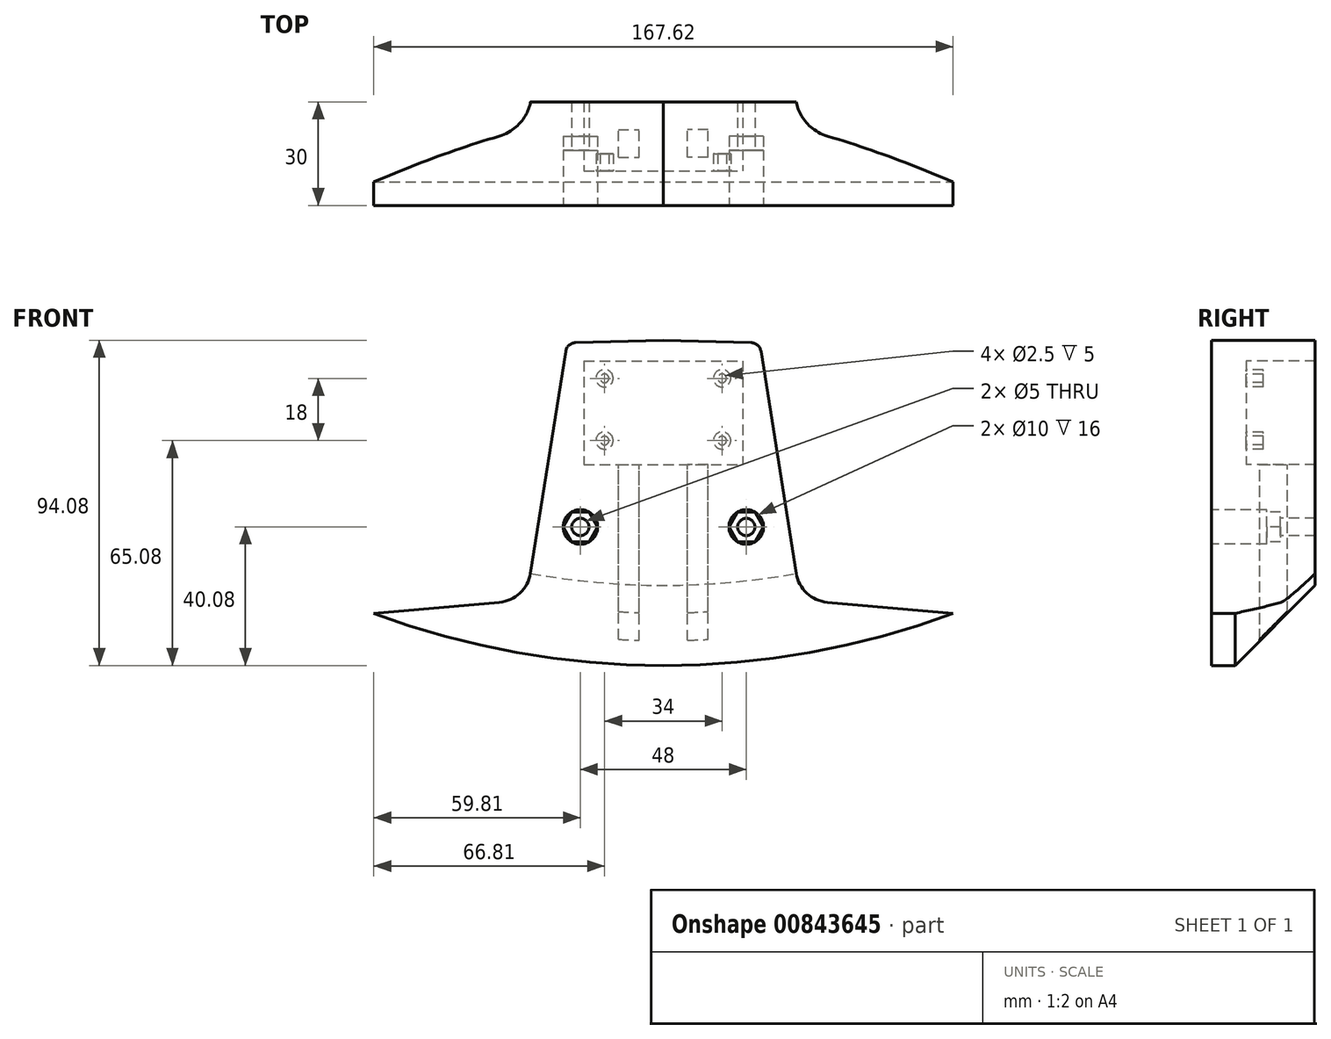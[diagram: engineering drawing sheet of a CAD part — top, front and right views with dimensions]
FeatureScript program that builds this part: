
annotation { "Feature Type Name" : "Feature", "Feature Type Description" : "" }
export const myFeature = defineFeature(function(context is Context, id is Id, definition is map)
    precondition{}
    {
        {
            var Q0;
            Q0=qCreatedBy(makeId("Front.planeOp"),FACE);
            var sketch = newSketch(context, id + "F0", { "sketchPlane" : qUnion([Q0])});
            skLineSegment(sketch, "E0.0", {"start": v(0, 104) * mm, "end": v(-25.36, 103.34) * mm});
            skLineSegment(sketch, "E1.0", {"start": v(-28.25, 100.8) * mm, "end": v(-38.45, 36.6) * mm});
            skArc(sketch, "E2.0", {"start": v(-38.45, 36.6) * mm, "mid": v(-41.51, 30.86) * mm, "end": v(-47.46, 28.21) * mm});
            skLineSegment(sketch, "E3.0", {"start": v(-47.46, 28.21) * mm, "end": v(-83.81, 25.03) * mm});
            skArc(sketch, "E4.0", {"start": v(-83.81, 25.03) * mm, "mid": v(-89.03, 27.33) * mm, "end": v(-89.9, 32.97) * mm});
            skLineSegment(sketch, "E5.0", {"start": v(-89.9, 32.97) * mm, "end": v(-64.25, 103.44) * mm});
            skArc(sketch, "E6", {"start": v(-105.92, 7.32) * mm, "mid": v(-53.83, -7.13) * mm, "end": v(0, -12) * mm});
            skArc(sketch, "E7", {"start": v(-25.36, 103.34) * mm, "mid": v(-27.26, 102.6) * mm, "end": v(-28.25, 100.8) * mm});
            skArc(sketch, "E8", {"start": v(-120, 37.98) * mm, "mid": v(-119.26, 19.76) * mm, "end": v(-105.92, 7.32) * mm});
            skLineSegment(sketch, "E9", {"start": v(-92.44, 113.7) * mm, "end": v(-64.25, 103.44) * mm});
            skArc(sketch, "E10.MirrorCS", {"start": v(25.36, 103.34) * mm, "mid": v(27.26, 102.6) * mm, "end": v(28.25, 100.8) * mm});
            skArc(sketch, "E11.MirrorCS", {"start": v(120, 37.98) * mm, "mid": v(119.26, 19.76) * mm, "end": v(105.92, 7.32) * mm});
            skLineSegment(sketch, "E12.MirrorCS", {"start": v(47.46, 28.21) * mm, "end": v(83.81, 25.03) * mm});
            skLineSegment(sketch, "E13.MirrorCS", {"start": v(0, 104) * mm, "end": v(25.36, 103.34) * mm});
            skLineSegment(sketch, "E14.MirrorCS", {"start": v(28.25, 100.8) * mm, "end": v(38.45, 36.6) * mm});
            skArc(sketch, "E15.MirrorCS", {"start": v(83.81, 25.03) * mm, "mid": v(89.03, 27.33) * mm, "end": v(89.9, 32.97) * mm});
            skArc(sketch, "E16.MirrorCS", {"start": v(38.45, 36.6) * mm, "mid": v(41.51, 30.86) * mm, "end": v(47.46, 28.21) * mm});
            skLineSegment(sketch, "E17.MirrorCS", {"start": v(89.9, 32.97) * mm, "end": v(64.25, 103.44) * mm});
            skArc(sketch, "E18.MirrorCS", {"start": v(105.92, 7.32) * mm, "mid": v(53.83, -7.13) * mm, "end": v(0, -12) * mm});
            skLineSegment(sketch, "E19.MirrorCS", {"start": v(92.44, 113.7) * mm, "end": v(64.25, 103.44) * mm});
            skLineSegment(sketch, "E20", {"start": v(-92.44, 113.7) * mm, "end": v(-120, 37.98) * mm});
            skLineSegment(sketch, "E21.MirrorCS", {"start": v(92.44, 113.7) * mm, "end": v(120, 37.98) * mm});
            skPoint(sketch, "E22", {"position": v(24, 50) * mm});
            skPoint(sketch, "E23", {"position": v(-24, 50) * mm});
            skLineSegment(sketch, "E24.bottom", {"start": v(-23, 98) * mm, "end": v(23, 98) * mm});
            skLineSegment(sketch, "E24.top", {"start": v(-23, 68) * mm, "end": v(23, 68) * mm});
            skLineSegment(sketch, "E24.left", {"start": v(-23, 98) * mm, "end": v(-23, 68) * mm});
            skLineSegment(sketch, "E24.right", {"start": v(23, 98) * mm, "end": v(23, 68) * mm});
            skCircle(sketch, "E25", {"center": v(17, 93) * mm, "radius": 2.5 * mm});
            skCircle(sketch, "E26", {"center": v(17, 75) * mm, "radius": 2.5 * mm});
            skCircle(sketch, "E27", {"center": v(-17, 93) * mm, "radius": 2.5 * mm});
            skCircle(sketch, "E28", {"center": v(-17, 75) * mm, "radius": 2.5 * mm});
            skCircle(sketch, "E29", {"center": v(17, 93) * mm, "radius": 1.25 * mm});
            skCircle(sketch, "E30", {"center": v(17, 75) * mm, "radius": 1.25 * mm});
            skCircle(sketch, "E31", {"center": v(-17, 75) * mm, "radius": 1.25 * mm});
            skCircle(sketch, "E32", {"center": v(-17, 93) * mm, "radius": 1.25 * mm});
            skPoint(sketch, "E33", {"position": v(0, 50) * mm});
            skArc(sketch, "E34", {"start": v(-83.81, 25.03) * mm, "mid": v(0, 9.92) * mm, "end": v(83.81, 25.03) * mm});
            skSolve(sketch);
        }
        {
            var Q0;
            Q0=makeQuery(id+"F0.imprint","IMPRINT",FACE,{"disambiguationData":[TD([[makeQuery(id+"F0.imprint","IMPRINT",EDGE,{"derivedFrom":sQuery(id+"F0.wireOp",EDGE,"E0.0")}),1.0]])]});
            var Q1;
            Q1=makeQuery(id+"F0.imprint","IMPRINT",FACE,{"disambiguationData":[TD([[makeQuery(id+"F0.imprint","IMPRINT",EDGE,{"derivedFrom":sQuery(id+"F0.wireOp",EDGE,"HJohPhqk-gpzc-Xpna-ZfSw-4RcINLic6Jsf")}),1.0]])]});
            var Q2;
            Q2=makeQuery(id+"F0.imprint","IMPRINT",FACE,{"disambiguationData":[TD([[makeQuery(id+"F0.imprint","IMPRINT",EDGE,{"derivedFrom":sQuery(id+"F0.wireOp",EDGE,"E3.0")}),1.0]])]});
            var Q3;
            Q3=makeQuery(id+"F0.imprint","IMPRINT",FACE,{"disambiguationData":[TD([[makeQuery(id+"F0.imprint","IMPRINT",EDGE,{"derivedFrom":sQuery(id+"F0.wireOp",EDGE,"E24.bottom")}),-1.0]])]});
            var Q4;
            Q4=makeQuery(id+"F0.imprint","IMPRINT",FACE,{"disambiguationData":[TD([[makeQuery(id+"F0.imprint","IMPRINT",EDGE,{"derivedFrom":sQuery(id+"F0.wireOp",EDGE,"E25")}),1.0]])]});
            var Q5;
            Q5=makeQuery(id+"F0.imprint","IMPRINT",FACE,{"disambiguationData":[TD([[makeQuery(id+"F0.imprint","IMPRINT",EDGE,{"derivedFrom":sQuery(id+"F0.wireOp",EDGE,"E26")}),1.0]])]});
            var Q6;
            Q6=makeQuery(id+"F0.imprint","IMPRINT",FACE,{"disambiguationData":[TD([[makeQuery(id+"F0.imprint","IMPRINT",EDGE,{"derivedFrom":sQuery(id+"F0.wireOp",EDGE,"E27")}),1.0]])]});
            var Q7;
            Q7=makeQuery(id+"F0.imprint","IMPRINT",FACE,{"disambiguationData":[TD([[makeQuery(id+"F0.imprint","IMPRINT",EDGE,{"derivedFrom":sQuery(id+"F0.wireOp",EDGE,"E28")}),1.0]])]});
            var Q8;
            Q8=makeQuery(id+"F0.imprint","IMPRINT",FACE,{"disambiguationData":[TD([[makeQuery(id+"F0.imprint","IMPRINT",EDGE,{"derivedFrom":sQuery(id+"F0.wireOp",EDGE,"E29")}),1.0]])]});
            var Q9;
            Q9=makeQuery(id+"F0.imprint","IMPRINT",FACE,{"disambiguationData":[TD([[makeQuery(id+"F0.imprint","IMPRINT",EDGE,{"derivedFrom":sQuery(id+"F0.wireOp",EDGE,"E32")}),1.0]])]});
            var Q10;
            Q10=makeQuery(id+"F0.imprint","IMPRINT",FACE,{"disambiguationData":[TD([[makeQuery(id+"F0.imprint","IMPRINT",EDGE,{"derivedFrom":sQuery(id+"F0.wireOp",EDGE,"E31")}),1.0]])]});
            var Q11;
            Q11=makeQuery(id+"F0.imprint","IMPRINT",FACE,{"disambiguationData":[TD([[makeQuery(id+"F0.imprint","IMPRINT",EDGE,{"derivedFrom":sQuery(id+"F0.wireOp",EDGE,"E30")}),1.0]])]});
            var Q12;
            Q12=makeQuery(id+"F0.imprint","IMPRINT",FACE,{"disambiguationData":[TD([[makeQuery(id+"F0.imprint","IMPRINT",EDGE,{"derivedFrom":sQuery(id+"F0.wireOp",EDGE,"E4.0")}),1.0]])]});
            extrude(context, id + "F1", {"entities" : qUnion([Q0, Q1, Q2, Q3, Q4, Q5, Q6, Q7, Q8, Q9, Q10, Q11, Q12]), "depth" : 10 * mm, "offsetDistance" : 25 * mm});
        }
        {
            var Q0;
            Q0=makeQuery(id+"F0.imprint","IMPRINT",FACE,{"disambiguationData":[TD([[makeQuery(id+"F0.imprint","IMPRINT",EDGE,{"derivedFrom":sQuery(id+"F0.wireOp",EDGE,"E0.0")}),1.0]])]});
            var Q1;
            {var subQ0=sQuery(id+"F0.wireOp",EDGE,"cf86e61c-85d1-4c12-8933-aeed4f83f32b.5");Q1=makeQuery(id+"F0.imprint","IMPRINT",FACE,{"disambiguationData":[TD([[makeQuery(id+"F0.imprint","IMPRINT",EDGE,{"derivedFrom":subQ0}),1.0]])]});}
            var Q2;
            {var subQ0=sQuery(id+"F0.wireOp",EDGE,"cf86e61c-85d1-4c12-8933-aeed4f83f32b.4");Q2=makeQuery(id+"F0.imprint","IMPRINT",FACE,{"disambiguationData":[TD([[makeQuery(id+"F0.imprint","IMPRINT",EDGE,{"derivedFrom":subQ0}),1.0]])]});}
            var Q3;
            {var subQ0=sQuery(id+"F0.wireOp",EDGE,"cf86e61c-85d1-4c12-8933-aeed4f83f32b.3");Q3=makeQuery(id+"F0.imprint","IMPRINT",FACE,{"disambiguationData":[TD([[makeQuery(id+"F0.imprint","IMPRINT",EDGE,{"derivedFrom":subQ0}),1.0]])]});}
            var Q4;
            {var subQ0=sQuery(id+"F0.wireOp",EDGE,"cf86e61c-85d1-4c12-8933-aeed4f83f32b.2");Q4=makeQuery(id+"F0.imprint","IMPRINT",FACE,{"disambiguationData":[TD([[makeQuery(id+"F0.imprint","IMPRINT",EDGE,{"derivedFrom":subQ0}),1.0]])]});}
            var Q5;
            {var subQ0=sQuery(id+"F0.wireOp",EDGE,"cf86e61c-85d1-4c12-8933-aeed4f83f32b.1");Q5=makeQuery(id+"F0.imprint","IMPRINT",FACE,{"disambiguationData":[TD([[makeQuery(id+"F0.imprint","IMPRINT",EDGE,{"derivedFrom":subQ0}),1.0]])]});}
            var Q6;
            {var subQ0=sQuery(id+"F0.wireOp",EDGE,"cf86e61c-85d1-4c12-8933-aeed4f83f32b.0");Q6=makeQuery(id+"F0.imprint","IMPRINT",FACE,{"disambiguationData":[TD([[makeQuery(id+"F0.imprint","IMPRINT",EDGE,{"derivedFrom":subQ0}),1.0]])]});}
            var Q7;
            {var subQ0=sQuery(id+"F0.wireOp",EDGE,"706c0b02-b9e9-40f9-bfac-7884581452ce0.MirrorCS");Q7=makeQuery(id+"F0.imprint","IMPRINT",FACE,{"disambiguationData":[TD([[makeQuery(id+"F0.imprint","IMPRINT",EDGE,{"derivedFrom":subQ0}),-1.0]])]});}
            var Q8;
            {var subQ0=sQuery(id+"F0.wireOp",EDGE,"7a833f0e-f727-4cb5-978e-7dddbb58226f0.MirrorCS");Q8=makeQuery(id+"F0.imprint","IMPRINT",FACE,{"disambiguationData":[TD([[makeQuery(id+"F0.imprint","IMPRINT",EDGE,{"derivedFrom":subQ0}),-1.0]])]});}
            var Q9;
            {var subQ0=sQuery(id+"F0.wireOp",EDGE,"fe4e47a0-1d68-48fd-ac7b-38c3e0d728ad0.MirrorCS");Q9=makeQuery(id+"F0.imprint","IMPRINT",FACE,{"disambiguationData":[TD([[makeQuery(id+"F0.imprint","IMPRINT",EDGE,{"derivedFrom":subQ0}),-1.0]])]});}
            var Q10;
            {var subQ0=sQuery(id+"F0.wireOp",EDGE,"510ec254-f475-4ab2-a435-2ccb126c0d140.MirrorCS");Q10=makeQuery(id+"F0.imprint","IMPRINT",FACE,{"disambiguationData":[TD([[makeQuery(id+"F0.imprint","IMPRINT",EDGE,{"derivedFrom":subQ0}),-1.0]])]});}
            var Q11;
            {var subQ0=sQuery(id+"F0.wireOp",EDGE,"c91b2912-07e7-41aa-bb4a-075838b2188d0.MirrorCS");Q11=makeQuery(id+"F0.imprint","IMPRINT",FACE,{"disambiguationData":[TD([[makeQuery(id+"F0.imprint","IMPRINT",EDGE,{"derivedFrom":subQ0}),-1.0]])]});}
            var Q12;
            {var subQ0=sQuery(id+"F0.wireOp",EDGE,"ac09b3a3-0592-4c97-b061-bd22dbb838b10.MirrorCS");Q12=makeQuery(id+"F0.imprint","IMPRINT",FACE,{"disambiguationData":[TD([[makeQuery(id+"F0.imprint","IMPRINT",EDGE,{"derivedFrom":subQ0}),-1.0]])]});}
            extrude(context, id + "F2", {"entities" : qUnion([Q0, Q1, Q2, Q3, Q4, Q5, Q6, Q7, Q8, Q9, Q10, Q11, Q12]), "operationType" : NewBodyOperationType.ADD, "oppositeDirection" : true, "depth" : 20 * mm, "offsetDistance" : 25 * mm});
        }
        {
            var Q0;
            Q0=makeQuery(id+"F1.opExtrude","CAP_FACE",FACE,{"disambiguationData":[OSD([sQuery(id+"F0.wireOp",EDGE,"E0.0"),sQuery(id+"F0.wireOp",EDGE,"E1.0"),sQuery(id+"F0.wireOp",EDGE,"E2.0"),sQuery(id+"F0.wireOp",EDGE,"E3.0"),sQuery(id+"F0.wireOp",EDGE,"E4.0"),sQuery(id+"F0.wireOp",EDGE,"E5.0"),sQuery(id+"F0.wireOp",EDGE,"E6"),sQuery(id+"F0.wireOp",EDGE,"E7"),sQuery(id+"F0.wireOp",EDGE,"E8"),sQuery(id+"F0.wireOp",EDGE,"E9"),sQuery(id+"F0.wireOp",EDGE,"E10.MirrorCS"),sQuery(id+"F0.wireOp",EDGE,"E11.MirrorCS"),sQuery(id+"F0.wireOp",EDGE,"E12.MirrorCS"),sQuery(id+"F0.wireOp",EDGE,"E13.MirrorCS"),sQuery(id+"F0.wireOp",EDGE,"E14.MirrorCS"),sQuery(id+"F0.wireOp",EDGE,"E15.MirrorCS"),sQuery(id+"F0.wireOp",EDGE,"E16.MirrorCS"),sQuery(id+"F0.wireOp",EDGE,"E17.MirrorCS"),sQuery(id+"F0.wireOp",EDGE,"E18.MirrorCS"),sQuery(id+"F0.wireOp",EDGE,"E19.MirrorCS"),sQuery(id+"F0.wireOp",EDGE,"E20"),sQuery(id+"F0.wireOp",EDGE,"E21.MirrorCS")])],"isStart":false});
            var sketch = newSketch(context, id + "F3", { "sketchPlane" : qUnion([Q0])});
            skPoint(sketch, "E35.0", {"position": v(-24, 50) * mm});
            skPoint(sketch, "E36.0", {"position": v(24, 50) * mm});
            skCircle(sketch, "E37", {"center": v(-24, 50) * mm, "radius": 5 * mm});
            skCircle(sketch, "E38", {"center": v(24, 50) * mm, "radius": 5 * mm});
            skCircle(sketch, "E39.cCircle", {"center": v(-24, 50) * mm, "radius": 4.33 * mm, "construction": true});
            skLineSegment(sketch, "E39.0", {"start": v(-21.5, 45.67) * mm, "end": v(-26.5, 45.67) * mm});
            skLineSegment(sketch, "E39.1", {"start": v(-26.5, 45.67) * mm, "end": v(-29, 50) * mm});
            skLineSegment(sketch, "E39.2", {"start": v(-29, 50) * mm, "end": v(-26.5, 54.33) * mm});
            skLineSegment(sketch, "E39.3", {"start": v(-26.5, 54.33) * mm, "end": v(-21.5, 54.33) * mm});
            skLineSegment(sketch, "E39.4", {"start": v(-21.5, 54.33) * mm, "end": v(-19, 50) * mm});
            skLineSegment(sketch, "E39.5", {"start": v(-19, 50) * mm, "end": v(-21.5, 45.67) * mm});
            skPoint(sketch, "E39.0.midPoint", {"position": v(-24, 45.67) * mm});
            skCircle(sketch, "E40.cCircle", {"center": v(24, 50) * mm, "radius": 4.33 * mm, "construction": true});
            skLineSegment(sketch, "E40.0", {"start": v(21.5, 54.33) * mm, "end": v(26.5, 54.33) * mm});
            skLineSegment(sketch, "E40.1", {"start": v(26.5, 54.33) * mm, "end": v(29, 50) * mm});
            skLineSegment(sketch, "E40.2", {"start": v(29, 50) * mm, "end": v(26.5, 45.67) * mm});
            skLineSegment(sketch, "E40.3", {"start": v(26.5, 45.67) * mm, "end": v(21.5, 45.67) * mm});
            skLineSegment(sketch, "E40.4", {"start": v(21.5, 45.67) * mm, "end": v(19, 50) * mm});
            skLineSegment(sketch, "E40.5", {"start": v(19, 50) * mm, "end": v(21.5, 54.33) * mm});
            skPoint(sketch, "E40.0.midPoint", {"position": v(24, 54.33) * mm});
            skCircle(sketch, "E41", {"center": v(-24, 50) * mm, "radius": 2.5 * mm});
            skCircle(sketch, "E42", {"center": v(24, 50) * mm, "radius": 2.5 * mm});
            skSolve(sketch);
        }
        {
            var Q0;
            Q0=makeQuery(id+"F3.imprint","IMPRINT",FACE,{"disambiguationData":[TD([[makeQuery(id+"F3.imprint","IMPRINT",EDGE,{"derivedFrom":sQuery(id+"F3.wireOp",EDGE,"E41")}),1.0]])]});
            var Q1;
            Q1=makeQuery(id+"F3.imprint","IMPRINT",FACE,{"disambiguationData":[TD([[makeQuery(id+"F3.imprint","IMPRINT",EDGE,{"derivedFrom":sQuery(id+"F3.wireOp",EDGE,"E42")}),1.0]])]});
            var Q2;
            Q2=makeQuery(id+"F2.opExtrude","CAP_FACE",FACE,{"disambiguationData":[OSD([sQuery(id+"F0.wireOp",EDGE,"E0.0"),sQuery(id+"F0.wireOp",EDGE,"E1.0"),sQuery(id+"F0.wireOp",EDGE,"E2.0"),sQuery(id+"F0.wireOp",EDGE,"E7"),sQuery(id+"F0.wireOp",EDGE,"HJohPhqk-gpzc-Xpna-ZfSw-4RcINLic6Jsf"),sQuery(id+"F0.wireOp",EDGE,"E10.MirrorCS"),sQuery(id+"F0.wireOp",EDGE,"E13.MirrorCS"),sQuery(id+"F0.wireOp",EDGE,"E14.MirrorCS"),sQuery(id+"F0.wireOp",EDGE,"E16.MirrorCS"),sQuery(id+"F0.wireOp",EDGE,"5OFpXgQB-ft6r-Mnft-UslJ-U83yNwtHumbk")])],"isStart":false});
            extrude(context, id + "F4", {"entities" : qUnion([Q0, Q1]), "operationType" : NewBodyOperationType.REMOVE, "endBound" : BoundingType.UP_TO_SURFACE, "oppositeDirection" : true, "depth" : 25 * mm, "endBoundEntityFace" : qUnion([Q2]), "offsetDistance" : 14 * mm});
        }
        {
            var Q0;
            Q0=makeQuery(id+"F3.imprint","IMPRINT",FACE,{"disambiguationData":[TD([[makeQuery(id+"F3.imprint","IMPRINT",EDGE,{"derivedFrom":sQuery(id+"F3.wireOp",EDGE,"E39.0")}),-1.0]])]});
            var Q1;
            Q1=makeQuery(id+"F3.imprint","IMPRINT",FACE,{"disambiguationData":[TD([[makeQuery(id+"F3.imprint","IMPRINT",EDGE,{"derivedFrom":sQuery(id+"F3.wireOp",EDGE,"E40.0")}),-1.0]])]});
            var Q2;
            Q2=makeQuery(id+"F2.opExtrude","CAP_FACE",FACE,{"disambiguationData":[OSD([sQuery(id+"F0.wireOp",EDGE,"E0.0"),sQuery(id+"F0.wireOp",EDGE,"E1.0"),sQuery(id+"F0.wireOp",EDGE,"E2.0"),sQuery(id+"F0.wireOp",EDGE,"E7"),sQuery(id+"F0.wireOp",EDGE,"HJohPhqk-gpzc-Xpna-ZfSw-4RcINLic6Jsf"),sQuery(id+"F0.wireOp",EDGE,"E10.MirrorCS"),sQuery(id+"F0.wireOp",EDGE,"E13.MirrorCS"),sQuery(id+"F0.wireOp",EDGE,"E14.MirrorCS"),sQuery(id+"F0.wireOp",EDGE,"E16.MirrorCS"),sQuery(id+"F0.wireOp",EDGE,"5OFpXgQB-ft6r-Mnft-UslJ-U83yNwtHumbk")])],"isStart":false});
            extrude(context, id + "F5", {"entities" : qUnion([Q0, Q1]), "operationType" : NewBodyOperationType.REMOVE, "endBound" : BoundingType.UP_TO_SURFACE, "oppositeDirection" : true, "depth" : 25 * mm, "endBoundEntityFace" : qUnion([Q2]), "hasOffset" : true, "offsetDistance" : 10 * mm});
        }
        {
            var Q0;
            {var subQ0=sQuery(id+"F3.wireOp",EDGE,"E39.1");Q0=makeQuery(id+"F3.imprint","IMPRINT",FACE,{"disambiguationData":[TD([[makeQuery(id+"F3.imprint","IMPRINT",EDGE,{"derivedFrom":subQ0}),1.0]])]});}
            var Q1;
            {var subQ0=sQuery(id+"F3.wireOp",EDGE,"E39.2");Q1=makeQuery(id+"F3.imprint","IMPRINT",FACE,{"disambiguationData":[TD([[makeQuery(id+"F3.imprint","IMPRINT",EDGE,{"derivedFrom":subQ0}),1.0]])]});}
            var Q2;
            {var subQ0=sQuery(id+"F3.wireOp",EDGE,"E39.3");Q2=makeQuery(id+"F3.imprint","IMPRINT",FACE,{"disambiguationData":[TD([[makeQuery(id+"F3.imprint","IMPRINT",EDGE,{"derivedFrom":subQ0}),1.0]])]});}
            var Q3;
            {var subQ0=sQuery(id+"F3.wireOp",EDGE,"E39.4");Q3=makeQuery(id+"F3.imprint","IMPRINT",FACE,{"disambiguationData":[TD([[makeQuery(id+"F3.imprint","IMPRINT",EDGE,{"derivedFrom":subQ0}),1.0]])]});}
            var Q4;
            {var subQ0=sQuery(id+"F3.wireOp",EDGE,"E39.5");Q4=makeQuery(id+"F3.imprint","IMPRINT",FACE,{"disambiguationData":[TD([[makeQuery(id+"F3.imprint","IMPRINT",EDGE,{"derivedFrom":subQ0}),1.0]])]});}
            var Q5;
            {var subQ0=sQuery(id+"F3.wireOp",EDGE,"E39.0");Q5=makeQuery(id+"F3.imprint","IMPRINT",FACE,{"disambiguationData":[TD([[makeQuery(id+"F3.imprint","IMPRINT",EDGE,{"derivedFrom":subQ0}),1.0]])]});}
            var Q6;
            {var subQ0=sQuery(id+"F3.wireOp",EDGE,"E40.5");Q6=makeQuery(id+"F3.imprint","IMPRINT",FACE,{"disambiguationData":[TD([[makeQuery(id+"F3.imprint","IMPRINT",EDGE,{"derivedFrom":subQ0}),1.0]])]});}
            var Q7;
            {var subQ0=sQuery(id+"F3.wireOp",EDGE,"E40.0");Q7=makeQuery(id+"F3.imprint","IMPRINT",FACE,{"disambiguationData":[TD([[makeQuery(id+"F3.imprint","IMPRINT",EDGE,{"derivedFrom":subQ0}),1.0]])]});}
            var Q8;
            {var subQ0=sQuery(id+"F3.wireOp",EDGE,"E40.1");Q8=makeQuery(id+"F3.imprint","IMPRINT",FACE,{"disambiguationData":[TD([[makeQuery(id+"F3.imprint","IMPRINT",EDGE,{"derivedFrom":subQ0}),1.0]])]});}
            var Q9;
            {var subQ0=sQuery(id+"F3.wireOp",EDGE,"E40.2");Q9=makeQuery(id+"F3.imprint","IMPRINT",FACE,{"disambiguationData":[TD([[makeQuery(id+"F3.imprint","IMPRINT",EDGE,{"derivedFrom":subQ0}),1.0]])]});}
            var Q10;
            {var subQ0=sQuery(id+"F3.wireOp",EDGE,"E40.3");Q10=makeQuery(id+"F3.imprint","IMPRINT",FACE,{"disambiguationData":[TD([[makeQuery(id+"F3.imprint","IMPRINT",EDGE,{"derivedFrom":subQ0}),1.0]])]});}
            var Q11;
            {var subQ0=sQuery(id+"F3.wireOp",EDGE,"E40.4");Q11=makeQuery(id+"F3.imprint","IMPRINT",FACE,{"disambiguationData":[TD([[makeQuery(id+"F3.imprint","IMPRINT",EDGE,{"derivedFrom":subQ0}),1.0]])]});}
            var Q12;
            Q12=makeQuery(id+"F5.boolean.opBoolean","COPY",FACE,{"derivedFrom":makeQuery(id+"F5.opExtrude","CAP_FACE",FACE,{"disambiguationData":[OSD([sQuery(id+"F3.wireOp",EDGE,"E39.0"),sQuery(id+"F3.wireOp",EDGE,"E39.1"),sQuery(id+"F3.wireOp",EDGE,"E39.2"),sQuery(id+"F3.wireOp",EDGE,"E39.3"),sQuery(id+"F3.wireOp",EDGE,"E39.4"),sQuery(id+"F3.wireOp",EDGE,"E39.5"),sQuery(id+"F3.wireOp",EDGE,"E41")])],"isStart":false})});
            extrude(context, id + "F6", {"entities" : qUnion([Q0, Q1, Q2, Q3, Q4, Q5, Q6, Q7, Q8, Q9, Q10, Q11]), "operationType" : NewBodyOperationType.REMOVE, "endBound" : BoundingType.UP_TO_SURFACE, "oppositeDirection" : true, "depth" : 25 * mm, "endBoundEntityFace" : qUnion([Q12]), "hasOffset" : true, "offsetDistance" : 4 * mm});
        }
        {
            var Q0;
            Q0=makeQuery(id+"F0.imprint","IMPRINT",FACE,{"disambiguationData":[TD([[makeQuery(id+"F0.imprint","IMPRINT",EDGE,{"derivedFrom":sQuery(id+"F0.wireOp",EDGE,"E25")}),1.0]])]});
            var Q1;
            Q1=makeQuery(id+"F0.imprint","IMPRINT",FACE,{"disambiguationData":[TD([[makeQuery(id+"F0.imprint","IMPRINT",EDGE,{"derivedFrom":sQuery(id+"F0.wireOp",EDGE,"E26")}),1.0]])]});
            var Q2;
            Q2=makeQuery(id+"F0.imprint","IMPRINT",FACE,{"disambiguationData":[TD([[makeQuery(id+"F0.imprint","IMPRINT",EDGE,{"derivedFrom":sQuery(id+"F0.wireOp",EDGE,"E28")}),1.0]])]});
            var Q3;
            Q3=makeQuery(id+"F0.imprint","IMPRINT",FACE,{"disambiguationData":[TD([[makeQuery(id+"F0.imprint","IMPRINT",EDGE,{"derivedFrom":sQuery(id+"F0.wireOp",EDGE,"E27")}),1.0]])]});
            extrude(context, id + "F7", {"entities" : qUnion([Q0, Q1, Q2, Q3]), "operationType" : NewBodyOperationType.ADD, "oppositeDirection" : true, "depth" : 5 * mm, "offsetDistance" : 25 * mm});
        }
        {
            var Q0;
            Q0=makeQuery(id+"F2.opExtrude","CAP_EDGE",EDGE,{"disambiguationData":[OSD([sQuery(id+"F0.wireOp",EDGE,"E34")])],"isStart":false});
            chamfer(context, id + "F8", {"entities" : qUnion([Q0]), "chamferType" : ChamferType.TWO_OFFSETS, "width1" : 23.2 * mm, "oppositeDirection" : false, "width2" : 23.2 * mm, "tangentPropagation" : true});
        }
        {
            var Q0;
            Q0=makeQuery(id+"F2.opExtrude","SWEPT_FACE",FACE,{"disambiguationData":[OSD([sQuery(id+"F0.wireOp",EDGE,"E24.top")])]});
            var sketch = newSketch(context, id + "F9", { "sketchPlane" : qUnion([Q0])});
            skLineSegment(sketch, "E43.bottom", {"start": v(13, 4) * mm, "end": v(7, 4) * mm});
            skLineSegment(sketch, "E43.top", {"start": v(13, 12) * mm, "end": v(7, 12) * mm});
            skLineSegment(sketch, "E43.left", {"start": v(13, 4) * mm, "end": v(13, 12) * mm});
            skLineSegment(sketch, "E43.right", {"start": v(7, 4) * mm, "end": v(7, 12) * mm});
            skLineSegment(sketch, "E44.MirrorCS", {"start": v(-7, 4) * mm, "end": v(-7, 12) * mm});
            skLineSegment(sketch, "E45.MirrorCS", {"start": v(-13, 4) * mm, "end": v(-7, 4) * mm});
            skLineSegment(sketch, "E46.MirrorCS", {"start": v(-13, 4) * mm, "end": v(-13, 12) * mm});
            skLineSegment(sketch, "E47.MirrorCS", {"start": v(-13, 12) * mm, "end": v(-7, 12) * mm});
            skSolve(sketch);
        }
        {
            var Q0;
            Q0=makeQuery(id+"F9.imprint","IMPRINT",FACE,{"disambiguationData":[TD([[makeQuery(id+"F9.imprint","IMPRINT",EDGE,{"derivedFrom":sQuery(id+"F9.wireOp",EDGE,"E43.bottom")}),-1.0]])]});
            var Q1;
            Q1=makeQuery(id+"F9.imprint","IMPRINT",FACE,{"disambiguationData":[TD([[makeQuery(id+"F9.imprint","IMPRINT",EDGE,{"derivedFrom":sQuery(id+"F9.wireOp",EDGE,"E44.MirrorCS")}),1.0]])]});
            var Q2;
            Q2=makeQuery(id+"F8.opChamfer","BLEND_FACE",FACE,{"disambiguationData":[OSD([sQuery(id+"F0.wireOp",EDGE,"E34")])]});
            extrude(context, id + "F10", {"entities" : qUnion([Q0, Q1]), "operationType" : NewBodyOperationType.REMOVE, "endBound" : BoundingType.UP_TO_SURFACE, "oppositeDirection" : true, "depth" : 25 * mm, "endBoundEntityFace" : qUnion([Q2]), "offsetDistance" : 25 * mm});
        }
    });
